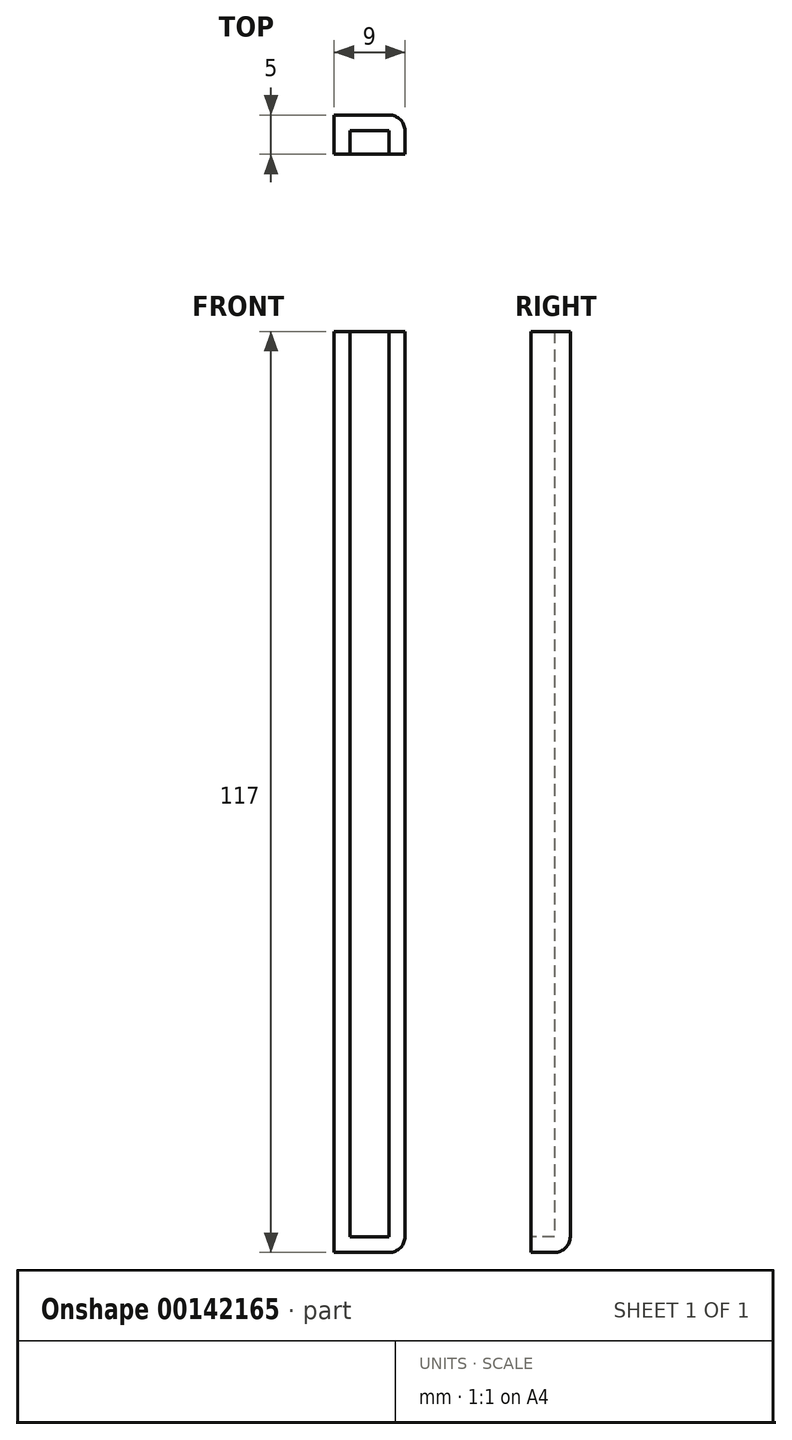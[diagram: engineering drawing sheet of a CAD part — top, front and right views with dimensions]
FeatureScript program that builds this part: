
annotation { "Feature Type Name" : "Feature", "Feature Type Description" : "" }
export const myFeature = defineFeature(function(context is Context, id is Id, definition is map)
    precondition{}
    {
        {
            var Q0;
            Q0=qCreatedBy(makeId("Top.planeOp"),FACE);
            var sketch = newSketch(context, id + "F0", { "sketchPlane" : qUnion([Q0])});
            skLineSegment(sketch, "E0", {"start": v(0, 0) * mm, "end": v(0, 5) * mm});
            skLineSegment(sketch, "E1", {"start": v(0, 5) * mm, "end": v(9, 5) * mm});
            skLineSegment(sketch, "E2", {"start": v(9, 5) * mm, "end": v(9, 0) * mm});
            skLineSegment(sketch, "E3", {"start": v(9, 0) * mm, "end": v(7, 0) * mm});
            skLineSegment(sketch, "E4", {"start": v(7, 0) * mm, "end": v(7, 3) * mm});
            skLineSegment(sketch, "E5", {"start": v(7, 3) * mm, "end": v(2, 3) * mm});
            skLineSegment(sketch, "E6", {"start": v(2, 3) * mm, "end": v(2, 0) * mm});
            skLineSegment(sketch, "E7", {"start": v(2, 0) * mm, "end": v(0, 0) * mm});
            skSolve(sketch);
        }
        {
            var Q0;
            Q0 = qSketchRegion(id + "F0", true);
            extrude(context, id + "F1", {"entities" : qUnion([Q0]), "depth" : 115 * mm});
        }
        {
            var Q0;
            Q0=qCreatedBy(makeId("Top.planeOp"),FACE);
            var sketch = newSketch(context, id + "F2", { "sketchPlane" : qUnion([Q0])});
            skLineSegment(sketch, "E8.bottom", {"start": v(0, 0) * mm, "end": v(9, 0) * mm});
            skLineSegment(sketch, "E8.top", {"start": v(0, 5) * mm, "end": v(9, 5) * mm});
            skLineSegment(sketch, "E8.left", {"start": v(0, 0) * mm, "end": v(0, 5) * mm});
            skLineSegment(sketch, "E8.right", {"start": v(9, 0) * mm, "end": v(9, 5) * mm});
            skSolve(sketch);
        }
        {
            var Q0;
            Q0 = qSketchRegion(id + "F2", true);
            extrude(context, id + "F3", {"entities" : qUnion([Q0]), "operationType" : NewBodyOperationType.ADD, "oppositeDirection" : true, "depth" : 2 * mm});
        }
        {
            var Q0;
            Q0=makeQuery(id+"F3.opExtrude","CAP_EDGE",EDGE,{"disambiguationData":[OSD([sQuery(id+"F2.wireOp",EDGE,"E8.top")])],"isStart":false});
            var Q1;
            Q1=makeQuery(id+"F3.boolean.opBoolean","MERGE",EDGE,{"derivedFrom":[makeQuery(id+"F1.opExtrude","SWEPT_EDGE",EDGE,{"disambiguationData":[OSD([sQuery(id+"F0.wireOp",EDGE,"E1"),sQuery(id+"F0.wireOp",EDGE,"E2")])]}),makeQuery(id+"F3.opExtrude","SWEPT_EDGE",EDGE,{"disambiguationData":[OSD([sQuery(id+"F2.wireOp",EDGE,"E8.top"),sQuery(id+"F2.wireOp",EDGE,"E8.right")])]})]});
            var Q2;
            Q2=makeQuery(id+"F3.opExtrude","CAP_EDGE",EDGE,{"disambiguationData":[OSD([sQuery(id+"F2.wireOp",EDGE,"E8.right")])],"isStart":false});
            fillet(context, id + "F4", {"entities" : qUnion([Q0, Q1, Q2]), "radius" : 2 * mm, "tangentPropagation" : true, "allowEdgeOverflow" : false});
        }
    });
